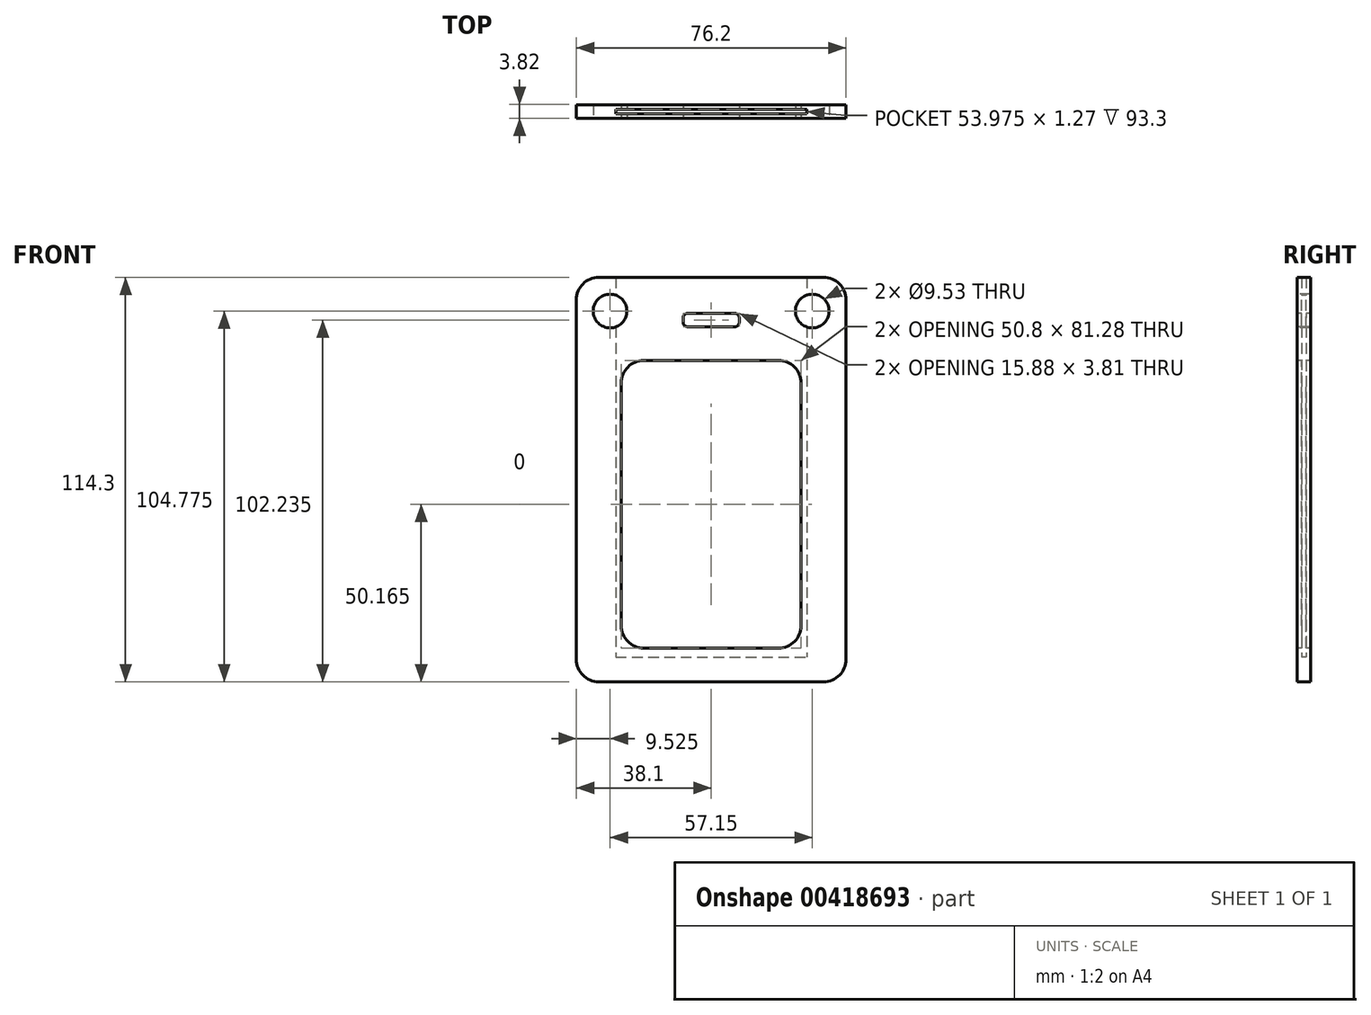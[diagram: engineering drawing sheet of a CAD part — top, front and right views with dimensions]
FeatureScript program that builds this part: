
annotation { "Feature Type Name" : "Feature", "Feature Type Description" : "" }
export const myFeature = defineFeature(function(context is Context, id is Id, definition is map)
    precondition{}
    {
        {
            var Q0;
            Q0=qCreatedBy(makeId("Front.planeOp"),FACE);
            var sketch = newSketch(context, id + "F0", { "sketchPlane" : qUnion([Q0])});
            skLineSegment(sketch, "E0.bottom", {"start": v(31.75, -57.15) * mm, "end": v(-31.75, -57.15) * mm});
            skLineSegment(sketch, "E0.top", {"start": v(31.75, 57.15) * mm, "end": v(-31.75, 57.15) * mm});
            skLineSegment(sketch, "E0.left", {"start": v(38.1, -50.8) * mm, "end": v(38.1, 50.8) * mm});
            skLineSegment(sketch, "E0.right", {"start": v(-38.1, -50.8) * mm, "end": v(-38.1, 50.8) * mm});
            skPoint(sketch, "E0.middle", {"position": v(0, 0) * mm});
            skPoint(sketch, "E1.visualSharp", {"position": v(-38.1, 57.15) * mm});
            skArc(sketch, "E1.filletArc", {"start": v(-31.75, 57.15) * mm, "mid": v(-36.24, 55.3) * mm, "end": v(-38.1, 50.8) * mm});
            skPoint(sketch, "E2.visualSharp", {"position": v(38.1, 57.15) * mm});
            skArc(sketch, "E2.filletArc", {"start": v(38.1, 50.8) * mm, "mid": v(36.24, 55.3) * mm, "end": v(31.75, 57.15) * mm});
            skPoint(sketch, "E3.visualSharp", {"position": v(38.1, -57.15) * mm});
            skArc(sketch, "E3.filletArc", {"start": v(31.75, -57.15) * mm, "mid": v(36.24, -55.3) * mm, "end": v(38.1, -50.8) * mm});
            skPoint(sketch, "E4.visualSharp", {"position": v(-38.1, -57.15) * mm});
            skArc(sketch, "E4.filletArc", {"start": v(-38.1, -50.8) * mm, "mid": v(-36.24, -55.3) * mm, "end": v(-31.75, -57.15) * mm});
            skSolve(sketch);
        }
        {
            var Q0;
            Q0 = qSketchRegion(id + "F0", true);
            extrude(context, id + "F1", {"entities" : qUnion([Q0]), "endBound" : BoundingType.SYMMETRIC, "depth" : 3.8 * mm});
        }
        {
            var Q0;
            Q0=makeQuery(id+"F1.opExtrude","CAP_FACE",FACE,{"disambiguationData":[OSD([sQuery(id+"F0.wireOp",EDGE,"E0.bottom"),sQuery(id+"F0.wireOp",EDGE,"E0.top"),sQuery(id+"F0.wireOp",EDGE,"E0.left"),sQuery(id+"F0.wireOp",EDGE,"E0.right")])],"isStart":false});
            var sketch = newSketch(context, id + "F2", { "sketchPlane" : qUnion([Q0])});
            skLineSegment(sketch, "E5.bottom", {"start": v(-19.05, 33.66) * mm, "end": v(19.05, 33.66) * mm});
            skLineSegment(sketch, "E5.top", {"start": v(-19.05, -47.63) * mm, "end": v(19.05, -47.63) * mm});
            skLineSegment(sketch, "E5.left", {"start": v(-25.4, 27.3) * mm, "end": v(-25.4, -41.28) * mm});
            skLineSegment(sketch, "E5.right", {"start": v(25.4, 27.3) * mm, "end": v(25.4, -41.28) * mm});
            skPoint(sketch, "E5.middle", {"position": v(0, -6.99) * mm});
            skPoint(sketch, "E6.visualSharp", {"position": v(-25.4, 33.66) * mm});
            skArc(sketch, "E6.filletArc", {"start": v(-19.05, 33.66) * mm, "mid": v(-23.54, 31.8) * mm, "end": v(-25.4, 27.3) * mm});
            skPoint(sketch, "E7.visualSharp", {"position": v(25.4, 33.66) * mm});
            skArc(sketch, "E7.filletArc", {"start": v(25.4, 27.3) * mm, "mid": v(23.54, 31.8) * mm, "end": v(19.05, 33.66) * mm});
            skPoint(sketch, "E8.visualSharp", {"position": v(25.4, -47.63) * mm});
            skArc(sketch, "E8.filletArc", {"start": v(19.05, -47.63) * mm, "mid": v(23.54, -45.77) * mm, "end": v(25.4, -41.28) * mm});
            skPoint(sketch, "E9.visualSharp", {"position": v(-25.4, -47.63) * mm});
            skArc(sketch, "E9.filletArc", {"start": v(-25.4, -41.28) * mm, "mid": v(-23.54, -45.77) * mm, "end": v(-19.05, -47.63) * mm});
            skSolve(sketch);
        }
        {
            var Q0;
            Q0 = qSketchRegion(id + "F2", true);
            extrude(context, id + "F3", {"entities" : qUnion([Q0]), "operationType" : NewBodyOperationType.REMOVE, "endBound" : BoundingType.THROUGH_ALL, "oppositeDirection" : true, "depth" : 25.4 * mm});
        }
        {
            var Q0;
            Q0=qCreatedBy(makeId("Front.planeOp"),FACE);
            var sketch = newSketch(context, id + "F4", { "sketchPlane" : qUnion([Q0])});
            skLineSegment(sketch, "E10.bottom", {"start": v(-26.99, 57.15) * mm, "end": v(26.99, 57.15) * mm});
            skLineSegment(sketch, "E10.top", {"start": v(-26.99, -50.17) * mm, "end": v(26.99, -50.17) * mm});
            skLineSegment(sketch, "E10.left", {"start": v(-26.99, 57.15) * mm, "end": v(-26.99, -50.17) * mm});
            skLineSegment(sketch, "E10.right", {"start": v(26.99, 57.15) * mm, "end": v(26.99, -50.17) * mm});
            skPoint(sketch, "E10.middle", {"position": v(0, 3.5) * mm});
            skSolve(sketch);
        }
        {
            var Q0;
            Q0 = qSketchRegion(id + "F4", true);
            extrude(context, id + "F5", {"entities" : qUnion([Q0]), "operationType" : NewBodyOperationType.REMOVE, "endBound" : BoundingType.SYMMETRIC, "oppositeDirection" : true, "depth" : 1.27 * mm});
        }
        {
            var Q0;
            Q0=makeQuery(id+"F1.opExtrude","CAP_FACE",FACE,{"disambiguationData":[OSD([sQuery(id+"F0.wireOp",EDGE,"E0.bottom"),sQuery(id+"F0.wireOp",EDGE,"E0.top"),sQuery(id+"F0.wireOp",EDGE,"E0.left"),sQuery(id+"F0.wireOp",EDGE,"E0.right"),sQuery(id+"F0.wireOp",EDGE,"E1.filletArc"),sQuery(id+"F0.wireOp",EDGE,"E2.filletArc"),sQuery(id+"F0.wireOp",EDGE,"E3.filletArc"),sQuery(id+"F0.wireOp",EDGE,"E4.filletArc")])],"isStart":false});
            var sketch = newSketch(context, id + "F6", { "sketchPlane" : qUnion([Q0])});
            skLineSegment(sketch, "E11.bottom", {"start": v(7.94, 43.18) * mm, "end": v(-7.94, 43.18) * mm});
            skLineSegment(sketch, "E11.top", {"start": v(7.94, 47) * mm, "end": v(-7.94, 47) * mm});
            skLineSegment(sketch, "E11.left", {"start": v(7.94, 43.18) * mm, "end": v(7.94, 47) * mm});
            skLineSegment(sketch, "E11.right", {"start": v(-7.94, 43.18) * mm, "end": v(-7.94, 47) * mm});
            skPoint(sketch, "E11.middle", {"position": v(0, 45.09) * mm});
            skSolve(sketch);
        }
        {
            var Q0;
            Q0 = qSketchRegion(id + "F6", true);
            extrude(context, id + "F7", {"entities" : qUnion([Q0]), "operationType" : NewBodyOperationType.REMOVE, "endBound" : BoundingType.THROUGH_ALL, "oppositeDirection" : true, "depth" : 25.4 * mm});
        }
        {
            var Q0;
            {var subQ0=sQuery(id+"F6.wireOp",EDGE,"E11.top");var subQ1=sQuery(id+"F6.wireOp",EDGE,"E11.right");Q0=makeQuery(id+"F7.boolean.opBoolean","COPY",EDGE,{"disambiguationData":[TD([makeQuery(id+"F5.boolean.opBoolean","COPY",FACE,{"derivedFrom":makeQuery(id+"F5.opExtrude","CAP_FACE",FACE,{"disambiguationData":[OSD([sQuery(id+"F4.wireOp",EDGE,"E10.bottom"),sQuery(id+"F4.wireOp",EDGE,"E10.top"),sQuery(id+"F4.wireOp",EDGE,"E10.left"),sQuery(id+"F4.wireOp",EDGE,"E10.right")])],"isStart":true})})])],"derivedFrom":makeQuery(id+"F7.opExtrude","SWEPT_EDGE",EDGE,{"disambiguationData":[OSD([subQ0,subQ1])]})});}
            var Q1;
            {var subQ0=sQuery(id+"F6.wireOp",EDGE,"E11.right");var subQ1=sQuery(id+"F6.wireOp",EDGE,"E11.top");Q1=makeQuery(id+"F7.boolean.opBoolean","COPY",EDGE,{"disambiguationData":[TD([makeQuery(id+"F5.boolean.opBoolean","COPY",FACE,{"derivedFrom":makeQuery(id+"F5.opExtrude","CAP_FACE",FACE,{"disambiguationData":[OSD([sQuery(id+"F4.wireOp",EDGE,"E10.bottom"),sQuery(id+"F4.wireOp",EDGE,"E10.top"),sQuery(id+"F4.wireOp",EDGE,"E10.left"),sQuery(id+"F4.wireOp",EDGE,"E10.right")])],"isStart":false})})])],"derivedFrom":makeQuery(id+"F7.opExtrude","SWEPT_EDGE",EDGE,{"disambiguationData":[OSD([subQ1,subQ0])]})});}
            var Q2;
            {var subQ0=sQuery(id+"F6.wireOp",EDGE,"E11.top");var subQ1=sQuery(id+"F6.wireOp",EDGE,"E11.left");Q2=makeQuery(id+"F7.boolean.opBoolean","COPY",EDGE,{"disambiguationData":[TD([makeQuery(id+"F5.boolean.opBoolean","COPY",FACE,{"derivedFrom":makeQuery(id+"F5.opExtrude","CAP_FACE",FACE,{"disambiguationData":[OSD([sQuery(id+"F4.wireOp",EDGE,"E10.bottom"),sQuery(id+"F4.wireOp",EDGE,"E10.top"),sQuery(id+"F4.wireOp",EDGE,"E10.left"),sQuery(id+"F4.wireOp",EDGE,"E10.right")])],"isStart":false})})])],"derivedFrom":makeQuery(id+"F7.opExtrude","SWEPT_EDGE",EDGE,{"disambiguationData":[OSD([subQ0,subQ1])]})});}
            var Q3;
            {var subQ0=sQuery(id+"F6.wireOp",EDGE,"E11.top");var subQ1=sQuery(id+"F6.wireOp",EDGE,"E11.left");Q3=makeQuery(id+"F7.boolean.opBoolean","COPY",EDGE,{"disambiguationData":[TD([makeQuery(id+"F5.boolean.opBoolean","COPY",FACE,{"derivedFrom":makeQuery(id+"F5.opExtrude","CAP_FACE",FACE,{"disambiguationData":[OSD([sQuery(id+"F4.wireOp",EDGE,"E10.bottom"),sQuery(id+"F4.wireOp",EDGE,"E10.top"),sQuery(id+"F4.wireOp",EDGE,"E10.left"),sQuery(id+"F4.wireOp",EDGE,"E10.right")])],"isStart":true})})])],"derivedFrom":makeQuery(id+"F7.opExtrude","SWEPT_EDGE",EDGE,{"disambiguationData":[OSD([subQ0,subQ1])]})});}
            var Q4;
            {var subQ0=sQuery(id+"F6.wireOp",EDGE,"E11.bottom");var subQ1=sQuery(id+"F6.wireOp",EDGE,"E11.left");Q4=makeQuery(id+"F7.boolean.opBoolean","COPY",EDGE,{"disambiguationData":[TD([makeQuery(id+"F5.boolean.opBoolean","COPY",FACE,{"derivedFrom":makeQuery(id+"F5.opExtrude","CAP_FACE",FACE,{"disambiguationData":[OSD([sQuery(id+"F4.wireOp",EDGE,"E10.bottom"),sQuery(id+"F4.wireOp",EDGE,"E10.top"),sQuery(id+"F4.wireOp",EDGE,"E10.left"),sQuery(id+"F4.wireOp",EDGE,"E10.right")])],"isStart":true})})])],"derivedFrom":makeQuery(id+"F7.opExtrude","SWEPT_EDGE",EDGE,{"disambiguationData":[OSD([subQ0,subQ1])]})});}
            var Q5;
            {var subQ0=sQuery(id+"F6.wireOp",EDGE,"E11.bottom");var subQ1=sQuery(id+"F6.wireOp",EDGE,"E11.left");Q5=makeQuery(id+"F7.boolean.opBoolean","COPY",EDGE,{"disambiguationData":[TD([makeQuery(id+"F5.boolean.opBoolean","COPY",FACE,{"derivedFrom":makeQuery(id+"F5.opExtrude","CAP_FACE",FACE,{"disambiguationData":[OSD([sQuery(id+"F4.wireOp",EDGE,"E10.bottom"),sQuery(id+"F4.wireOp",EDGE,"E10.top"),sQuery(id+"F4.wireOp",EDGE,"E10.left"),sQuery(id+"F4.wireOp",EDGE,"E10.right")])],"isStart":false})})])],"derivedFrom":makeQuery(id+"F7.opExtrude","SWEPT_EDGE",EDGE,{"disambiguationData":[OSD([subQ0,subQ1])]})});}
            var Q6;
            {var subQ0=sQuery(id+"F6.wireOp",EDGE,"E11.bottom");var subQ1=sQuery(id+"F6.wireOp",EDGE,"E11.right");Q6=makeQuery(id+"F7.boolean.opBoolean","COPY",EDGE,{"disambiguationData":[TD([makeQuery(id+"F5.boolean.opBoolean","COPY",FACE,{"derivedFrom":makeQuery(id+"F5.opExtrude","CAP_FACE",FACE,{"disambiguationData":[OSD([sQuery(id+"F4.wireOp",EDGE,"E10.bottom"),sQuery(id+"F4.wireOp",EDGE,"E10.top"),sQuery(id+"F4.wireOp",EDGE,"E10.left"),sQuery(id+"F4.wireOp",EDGE,"E10.right")])],"isStart":false})})])],"derivedFrom":makeQuery(id+"F7.opExtrude","SWEPT_EDGE",EDGE,{"disambiguationData":[OSD([subQ0,subQ1])]})});}
            var Q7;
            {var subQ0=sQuery(id+"F6.wireOp",EDGE,"E11.bottom");var subQ1=sQuery(id+"F6.wireOp",EDGE,"E11.right");Q7=makeQuery(id+"F7.boolean.opBoolean","COPY",EDGE,{"disambiguationData":[TD([makeQuery(id+"F5.boolean.opBoolean","COPY",FACE,{"derivedFrom":makeQuery(id+"F5.opExtrude","CAP_FACE",FACE,{"disambiguationData":[OSD([sQuery(id+"F4.wireOp",EDGE,"E10.bottom"),sQuery(id+"F4.wireOp",EDGE,"E10.top"),sQuery(id+"F4.wireOp",EDGE,"E10.left"),sQuery(id+"F4.wireOp",EDGE,"E10.right")])],"isStart":true})})])],"derivedFrom":makeQuery(id+"F7.opExtrude","SWEPT_EDGE",EDGE,{"disambiguationData":[OSD([subQ0,subQ1])]})});}
            fillet(context, id + "F8", {"entities" : qUnion([Q0, Q1, Q2, Q3, Q4, Q5, Q6, Q7]), "radius" : 1.27 * mm, "tangentPropagation" : true, "allowEdgeOverflow" : false});
        }
        {
            var Q0;
            Q0=makeQuery(id+"F1.opExtrude","CAP_FACE",FACE,{"disambiguationData":[OSD([sQuery(id+"F0.wireOp",EDGE,"E0.bottom"),sQuery(id+"F0.wireOp",EDGE,"E0.top"),sQuery(id+"F0.wireOp",EDGE,"E0.left"),sQuery(id+"F0.wireOp",EDGE,"E0.right"),sQuery(id+"F0.wireOp",EDGE,"E1.filletArc"),sQuery(id+"F0.wireOp",EDGE,"E2.filletArc"),sQuery(id+"F0.wireOp",EDGE,"E3.filletArc"),sQuery(id+"F0.wireOp",EDGE,"E4.filletArc")])],"isStart":false});
            var sketch = newSketch(context, id + "F9", { "sketchPlane" : qUnion([Q0])});
            skLineSegment(sketch, "E12", {"start": v(-38.1, 47.63) * mm, "end": v(38.1, 47.63) * mm, "construction": true});
            skCircle(sketch, "E13", {"center": v(-28.58, 47.63) * mm, "radius": 4.76 * mm});
            skCircle(sketch, "E14", {"center": v(28.58, 47.63) * mm, "radius": 4.76 * mm});
            skSolve(sketch);
        }
        {
            var Q0;
            Q0 = qSketchRegion(id + "F9", true);
            extrude(context, id + "F10", {"entities" : qUnion([Q0]), "operationType" : NewBodyOperationType.REMOVE, "endBound" : BoundingType.THROUGH_ALL, "oppositeDirection" : true, "depth" : 25.4 * mm});
        }
    });
